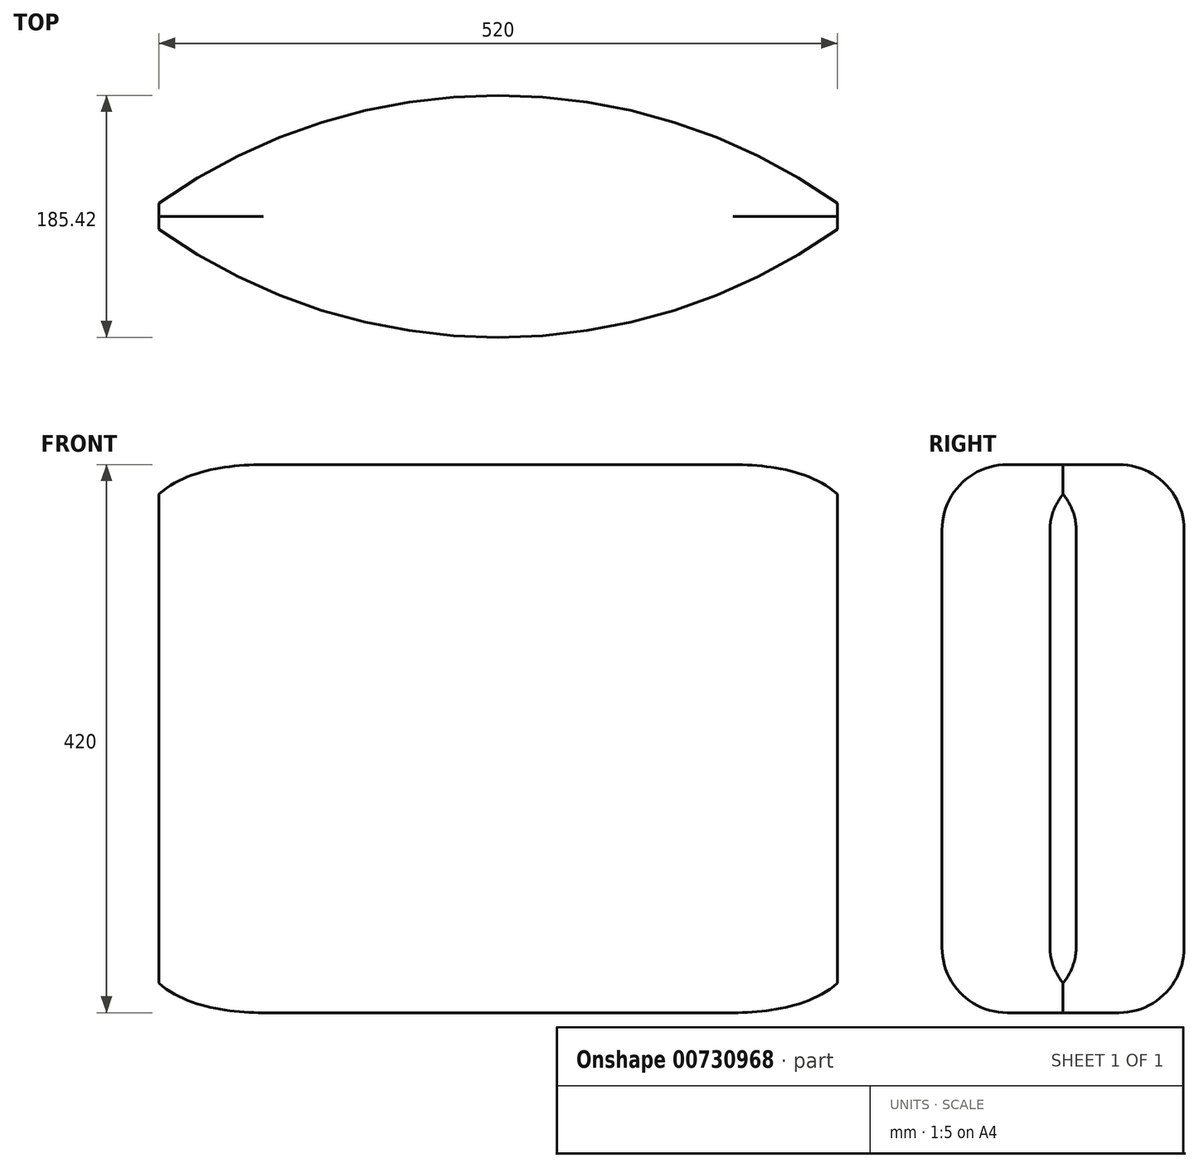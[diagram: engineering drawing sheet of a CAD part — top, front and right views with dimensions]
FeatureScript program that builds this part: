
annotation { "Feature Type Name" : "Feature", "Feature Type Description" : "" }
export const myFeature = defineFeature(function(context is Context, id is Id, definition is map)
    precondition{}
    {
        {
            var Q0;
            Q0=qCreatedBy(makeId("Top.planeOp"),FACE);
            var sketch = newSketch(context, id + "F0", { "sketchPlane" : qUnion([Q0])});
            skLineSegment(sketch, "E0.bottom", {"start": v(260, -10) * mm, "end": v(-260, -10) * mm});
            skLineSegment(sketch, "E0.top", {"start": v(260, 10) * mm, "end": v(-260, 10) * mm});
            skLineSegment(sketch, "E0.left", {"start": v(260, -10) * mm, "end": v(260, 10) * mm});
            skLineSegment(sketch, "E0.right", {"start": v(-260, -10) * mm, "end": v(-260, 10) * mm});
            skPoint(sketch, "E0.middle", {"position": v(0, 0) * mm});
            skArc(sketch, "E1", {"start": v(260, 10) * mm, "mid": v(0, 92.71) * mm, "end": v(-260, 10) * mm});
            skArc(sketch, "E2", {"start": v(-260, -10) * mm, "mid": v(0, -92.71) * mm, "end": v(260, -10) * mm});
            skSolve(sketch);
        }
        {
            var Q0;
            Q0=makeQuery(id+"F0.imprint","IMPRINT",FACE,{"disambiguationData":[TD([[makeQuery(id+"F0.imprint","IMPRINT",EDGE,{"derivedFrom":sQuery(id+"F0.wireOp",EDGE,"E0.bottom")}),1.0]])]});
            var Q1;
            Q1=makeQuery(id+"F0.imprint","IMPRINT",FACE,{"disambiguationData":[TD([[makeQuery(id+"F0.imprint","IMPRINT",EDGE,{"derivedFrom":sQuery(id+"F0.wireOp",EDGE,"E0.bottom")}),-1.0]])]});
            var Q2;
            Q2=makeQuery(id+"F0.imprint","IMPRINT",FACE,{"disambiguationData":[TD([[makeQuery(id+"F0.imprint","IMPRINT",EDGE,{"derivedFrom":sQuery(id+"F0.wireOp",EDGE,"E0.top")}),-1.0]])]});
            extrude(context, id + "F1", {"entities" : qUnion([Q0, Q1, Q2]), "depth" : 420 * mm, "offsetDistance" : 25 * mm});
        }
        {
            var Q0;
            Q0=makeQuery(id+"F1.opExtrude","CAP_EDGE",EDGE,{"disambiguationData":[OSD([sQuery(id+"F0.wireOp",EDGE,"E2")])],"isStart":false});
            var Q1;
            Q1=makeQuery(id+"F1.opExtrude","CAP_EDGE",EDGE,{"disambiguationData":[OSD([sQuery(id+"F0.wireOp",EDGE,"E1")])],"isStart":false});
            var Q2;
            Q2=makeQuery(id+"F1.opExtrude","CAP_EDGE",EDGE,{"disambiguationData":[OSD([sQuery(id+"F0.wireOp",EDGE,"E2")])],"isStart":true});
            var Q3;
            Q3=makeQuery(id+"F1.opExtrude","CAP_EDGE",EDGE,{"disambiguationData":[OSD([sQuery(id+"F0.wireOp",EDGE,"E1")])],"isStart":true});
            fillet(context, id + "F2", {"entities" : qUnion([Q0, Q1, Q2, Q3]), "radius" : 50 * mm, "tangentPropagation" : true, "allowEdgeOverflow" : false});
        }
    });
